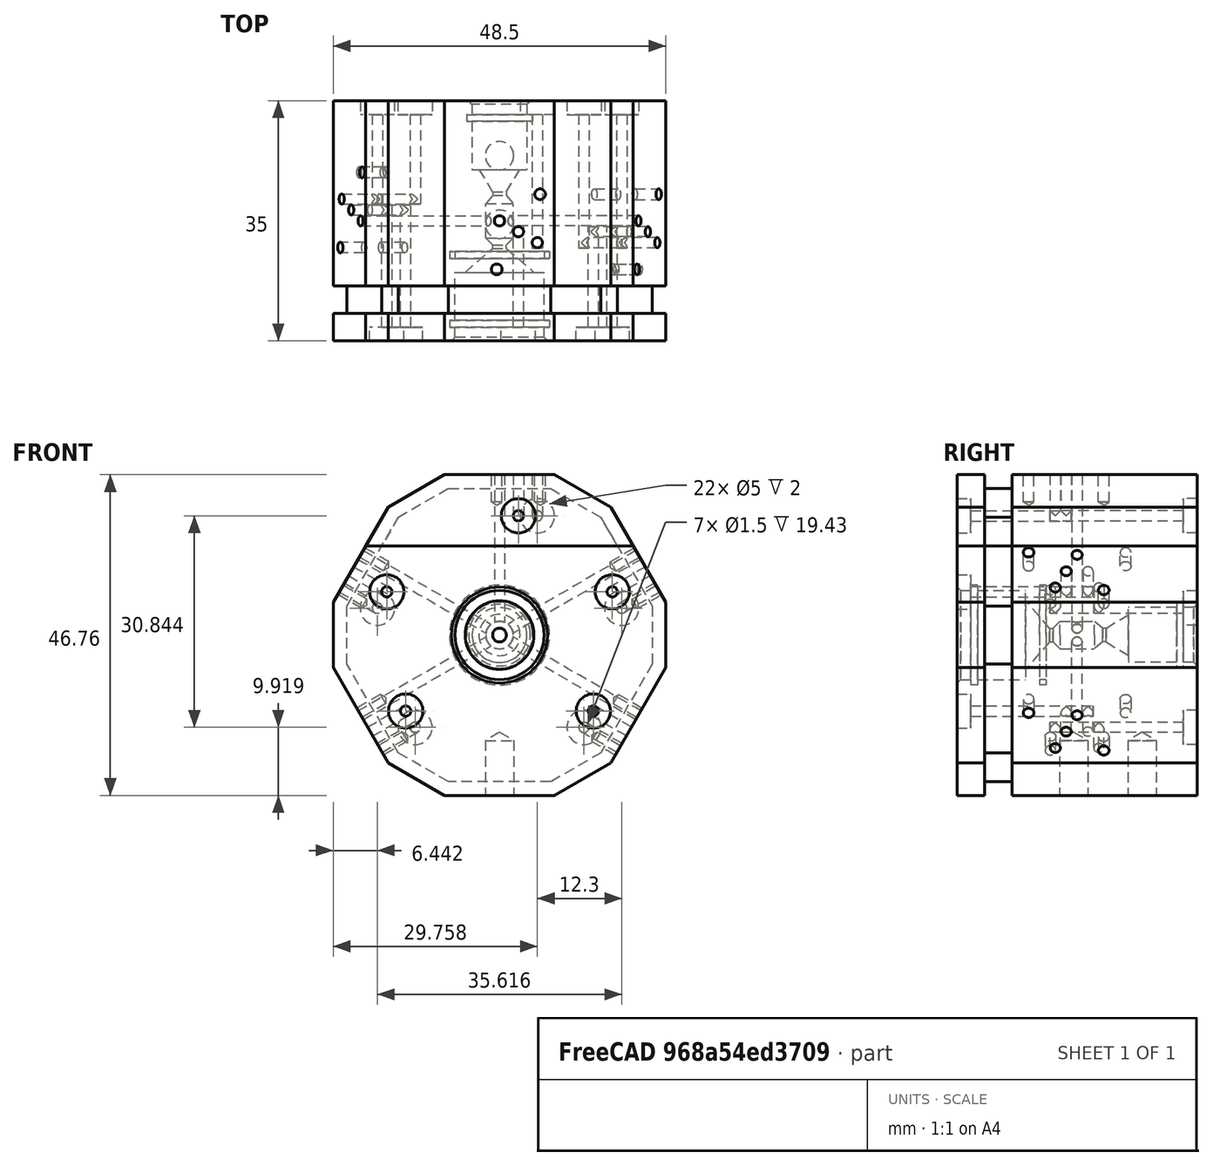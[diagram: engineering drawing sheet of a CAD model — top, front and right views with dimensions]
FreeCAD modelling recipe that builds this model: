
FCSTD DOCUMENT  (FreeCAD 0.18.4R)
Label: pre-flush
Comment: # 2020-08-05 14:49:47: read from <userpath>/repositories/sussex_neuro/Olfactometer/hardware/mechanics/from_raiser_et_al/nozzle_big.ipt
License: All rights reserved
LicenseURL: http://en.wikipedia.org/wiki/All_rights_reserved
objects: Part::Cylinder×6, Part::Feature×4, Part::Cut×4, Part::MultiFuse×3, App::FeaturePython×2, Part::Fuse×1, PartDesign::FeatureBase×1, PartDesign::Body×1, Part::Box×1
note: 21 computed .brp shape members not serialized (recipe doc carries the construction recipe); baked Part::Feature solids carry a one-line shape summary decoded from their .brp

FEATURE [Part::Feature] Part__Feature  label="main"
  shape: bbox 48.5 x 35 x 46.77 mm, 148 faces, 0 solids (baked)
FEATURE [Part::Feature] Part__Feature002  label="nozzle_small"
  Placement = pos=(0,2.5,0) rot=(-1,0,0;1.5708rad)
  shape: bbox 8 x 5 x 8 mm, 6 faces (baked)
FEATURE [Part::Feature] Part__Feature004  label="nozzle_big"
  Placement = pos=(0,-2.5,0) rot=(1,0,0;1.5708rad)
  shape: bbox 13 x 5 x 13 mm, 6 faces (baked)
FEATURE [Part::Feature] Part__Feature_solid  label="main (Solid)"
  shape: bbox 48.5 x 35 x 46.77 mm, 148 faces (baked)
FEATURE [Part::MultiFuse] Fusion  label="boddy_fusion_nozzles"
  Shapes = -> [Part__Feature002,Part__Feature004,Part__Feature_solid]
FEATURE [Part::Cylinder] Cylinder
  Angle = 360
  AttacherType = Attacher::AttachEngine3D
  Height = 4
  Placement = pos=(0,2,0) rot=(-1,0,0;1.5708rad)
  Radius = 5
FEATURE [Part::Cylinder] Cylinder001
  Angle = 360
  AttacherType = Attacher::AttachEngine3D
  Height = 11
  Placement = pos=(0,0,0) rot=(-1,0,0;1.5708rad)
  Radius = 4
FEATURE [Part::Fuse] Fusion001
  Base = -> Fusion
FEATURE [Part::Cylinder] Cylinder002
  Angle = 360
  AttacherType = Attacher::AttachEngine3D
  Height = 3
  Placement = pos=(0,-3,0) rot=(1,0,0;1.5708rad)
  Radius = 8
FEATURE [Part::Cylinder] Cylinder003
  Angle = 360
  AttacherType = Attacher::AttachEngine3D
  Height = 11
  Placement = pos=(0,0,0) rot=(1,0,0;1.5708rad)
  Radius = 6
FEATURE [Part::Cut] Cut
  Base = -> Cylinder
  Tool = -> Cylinder001
FEATURE [Part::Cut] Cut001
  Base = -> Cylinder002
  Tool = -> Cylinder003
FEATURE [Part::MultiFuse] Fusion002  label="join_cylinders_to_remove_gap"
  Shapes = -> [Fusion,Cut,Cut001]
FEATURE [PartDesign::FeatureBase] BaseFeature
  BaseFeature = -> Fusion002
FEATURE [PartDesign::Body] Body
  BaseFeature = -> Fusion002
  Group = -> [BaseFeature]
  Origin = -> Origin
  Tip = -> BaseFeature
FEATURE [App::FeaturePython] Dimension  # Draft dimension (typed FeaturePython)
  Diameter = false
  Dimline = (20.9801,-17.5,-0.0116531)
  Direction = (0,0,0)
  Distance = 13.9854
  End = (6.99466,-17.5,-0.0439505)
  Normal = (0,0,-1)
  Start = (-6.99074,-17.5,-0.076248)
FEATURE [App::FeaturePython] Dimension001  # Draft dimension (typed FeaturePython)
  Diameter = false
  Dimline = (19.4569,-16.5402,0.3547)
  Direction = (0,0,0)
  Distance = 12.9618
  End = (6.5,-16.5384,-1e-15)
  Normal = (0,0,1)
  Start = (-6.45693,-16.5366,-0.354704)
FEATURE [Part::Cylinder] Cylinder004
  Angle = 360
  AttacherType = Attacher::AttachEngine3D
  Height = 10
  Placement = pos=(0,0,0) rot=(1,0,0;1.5708rad)
  Radius = 8
FEATURE [Part::Cylinder] Cylinder005
  Angle = 360
  AttacherType = Attacher::AttachEngine3D
  Height = 12
  Placement = pos=(0,1,0) rot=(1,0,0;1.5708rad)
  Radius = 5.1
FEATURE [Part::Cut] Cut002
  Base = -> Cylinder004
  Placement = pos=(0,-7.5,0) rot=(0,0,1;0rad)
  Tool = -> Cylinder005
FEATURE [Part::MultiFuse] Fusion003  label="join_cylinder_to_fit_glass_tube"
  Shapes = -> [Cut002,Fusion002]
FEATURE [Part::Box] Box  label="Cube"
  AttacherType = Attacher::AttachEngine3D
  Height = 60
  Length = 60
  Placement = pos=(-27,-24,-47) rot=(0,0,1;0rad)
  Width = 50
FEATURE [Part::Cut] Cut003
  Base = -> Fusion003
  Tool = -> Box
